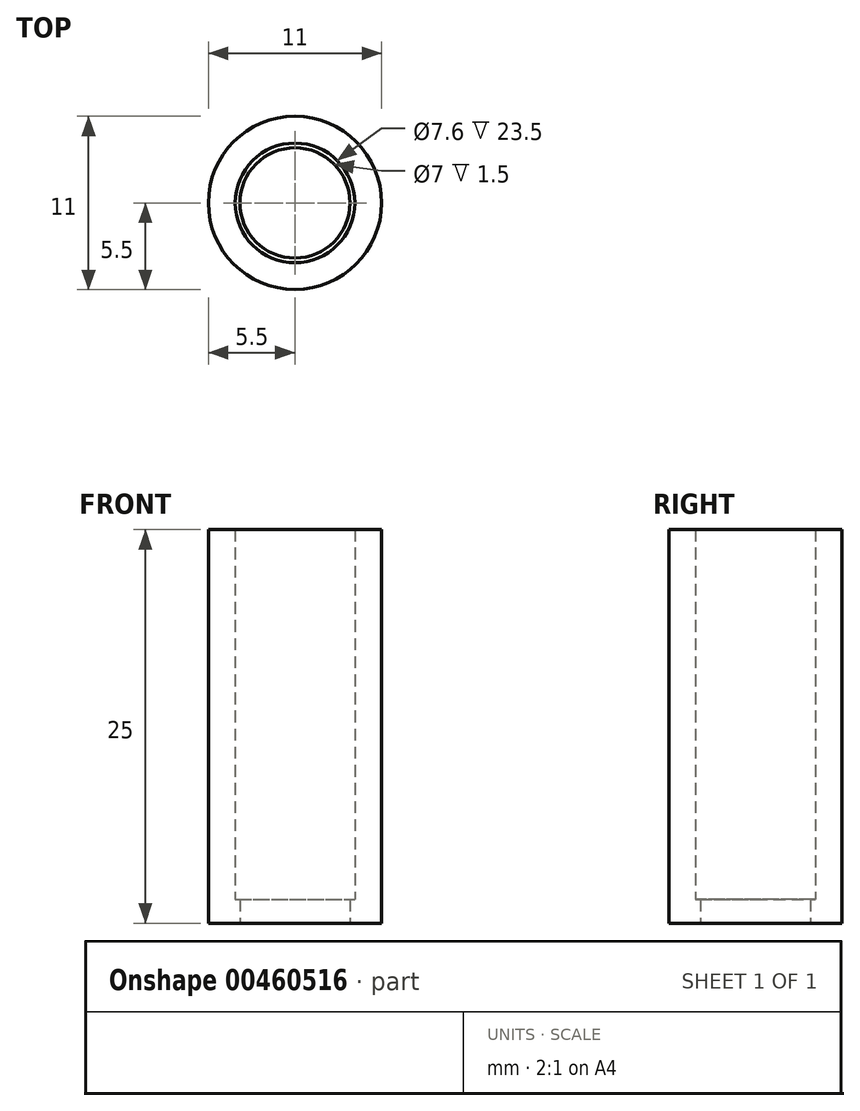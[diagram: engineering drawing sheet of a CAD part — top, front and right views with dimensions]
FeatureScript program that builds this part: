
annotation { "Feature Type Name" : "Feature", "Feature Type Description" : "" }
export const myFeature = defineFeature(function(context is Context, id is Id, definition is map)
    precondition{}
    {
        {
            var Q0;
            Q0=qCreatedBy(makeId("Top.planeOp"),FACE);
            var sketch = newSketch(context, id + "F0", { "sketchPlane" : qUnion([Q0])});
            skCircle(sketch, "E0", {"center": v(0, 0) * mm, "radius": 5.5 * mm});
            skCircle(sketch, "E1", {"center": v(0, 0) * mm, "radius": 3.8 * mm});
            skSolve(sketch);
        }
        {
            var Q0;
            Q0=qSketchRegion(id+"F0",true);
            extrude(context, id + "F1", {"entities" : qUnion([Q0]), "depth" : 25 * mm});
        }
        {
            var Q0;
            Q0=makeQuery(id+"F1.opExtrude","CAP_FACE",FACE,{"disambiguationData":[OSD([sQuery(id+"F0.wireOp",EDGE,"E0"),sQuery(id+"F0.wireOp",EDGE,"E1")])],"isStart":true});
            var sketch = newSketch(context, id + "F2", { "sketchPlane" : qUnion([Q0])});
            skCircle(sketch, "E2", {"center": v(0, 0) * mm, "radius": 3.5 * mm});
            skCircle(sketch, "E3", {"center": v(0, 0) * mm, "radius": 5.5 * mm});
            skSolve(sketch);
        }
        {
            var Q0;
            Q0 = qSketchRegion(id + "F2", true);
            extrude(context, id + "F3", {"entities" : qUnion([Q0]), "operationType" : NewBodyOperationType.ADD, "oppositeDirection" : true, "depth" : 1.5 * mm, "offsetDistance" : 25 * mm});
        }
    });
